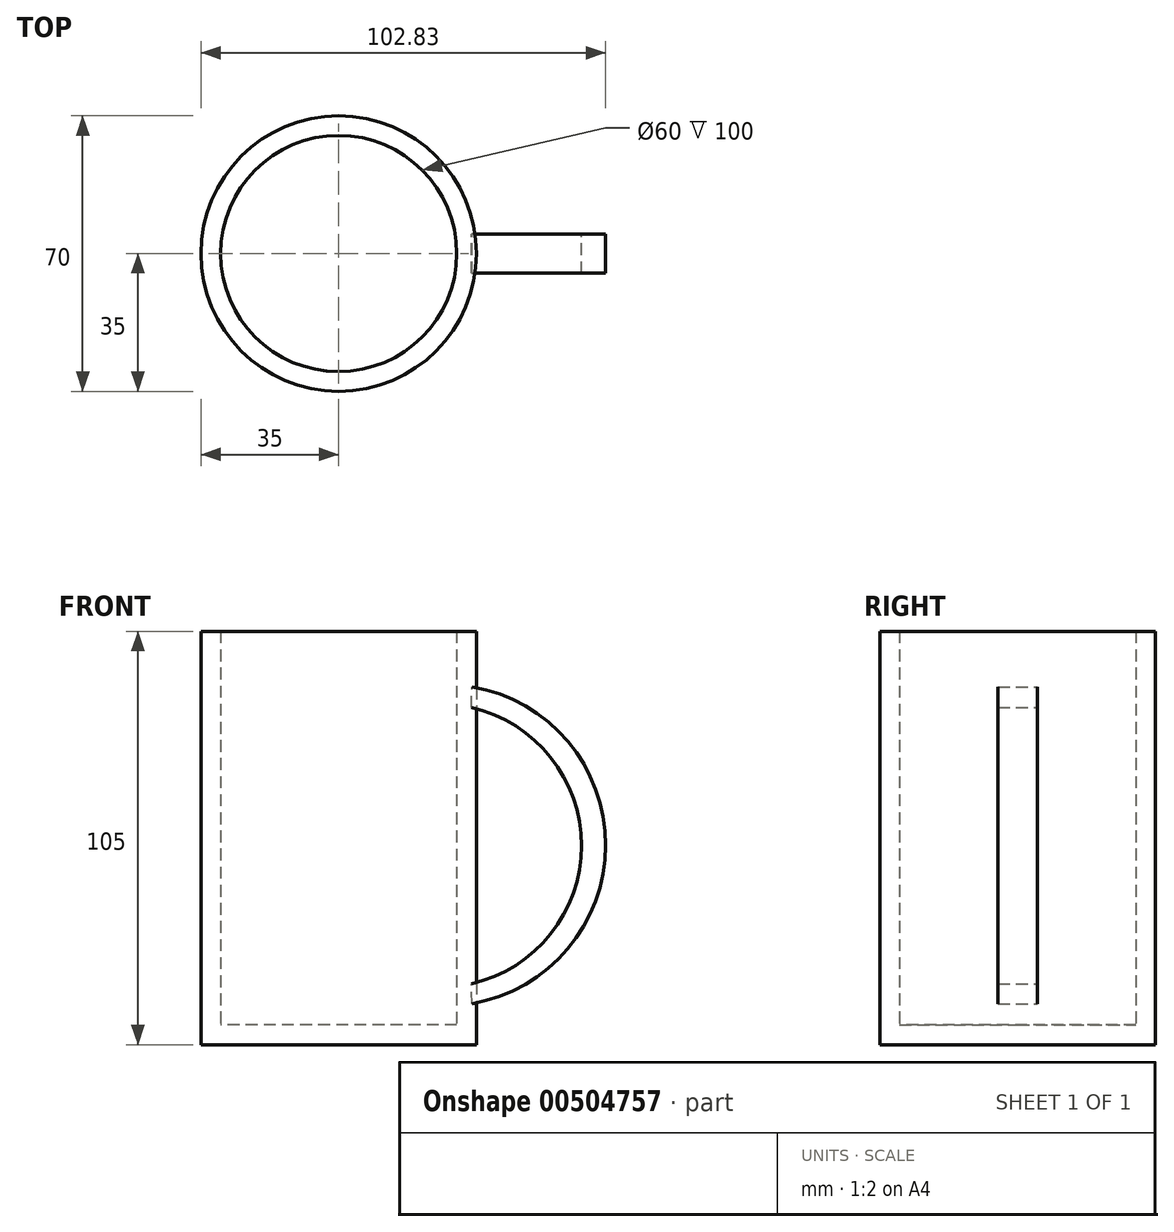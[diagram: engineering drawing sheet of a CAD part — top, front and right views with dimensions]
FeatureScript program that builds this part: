
annotation { "Feature Type Name" : "Feature", "Feature Type Description" : "" }
export const myFeature = defineFeature(function(context is Context, id is Id, definition is map)
    precondition{}
    {
        {
            var Q0;
            Q0=qCreatedBy(makeId("Top.planeOp"),FACE);
            var sketch = newSketch(context, id + "F0", { "sketchPlane" : qUnion([Q0])});
            skCircle(sketch, "E0", {"center": v(0, 0) * mm, "radius": 35 * mm});
            skSolve(sketch);
        }
        {
            var Q0;
            Q0 = qSketchRegion(id + "F0", true);
            extrude(context, id + "F1", {"entities" : qUnion([Q0]), "depth" : 5 * mm});
        }
        {
            var Q0;
            Q0=makeQuery(id+"F1.opExtrude","CAP_FACE",FACE,{"disambiguationData":[OSD([sQuery(id+"F0.wireOp",EDGE,"E0")])],"isStart":false});
            var sketch = newSketch(context, id + "F2", { "sketchPlane" : qUnion([Q0])});
            skCircle(sketch, "E1", {"center": v(0, 0) * mm, "radius": 35 * mm});
            skCircle(sketch, "E2", {"center": v(0, 0) * mm, "radius": 30 * mm});
            skSolve(sketch);
        }
        {
            var Q0;
            Q0 = qSketchRegion(id + "F2", true);
            extrude(context, id + "F3", {"entities" : qUnion([Q0]), "operationType" : NewBodyOperationType.ADD, "depth" : 100 * mm});
        }
        {
            var Q0;
            Q0=qCreatedBy(makeId("Front.planeOp"),FACE);
            var sketch = newSketch(context, id + "F4", { "sketchPlane" : qUnion([Q0])});
            skArc(sketch, "E3", {"start": v(33.72, 15.46) * mm, "mid": v(61.72, 50.56) * mm, "end": v(33.73, 85.66) * mm});
            skArc(sketch, "E4", {"start": v(33.82, 10.41) * mm, "mid": v(67.83, 50.65) * mm, "end": v(33.88, 90.94) * mm});
            skLineSegment(sketch, "E5", {"start": v(33.73, 85.66) * mm, "end": v(33.88, 90.94) * mm});
            skLineSegment(sketch, "E6", {"start": v(33.82, 10.41) * mm, "end": v(33.72, 15.46) * mm});
            skSolve(sketch);
        }
        {
            var Q0;
            Q0 = qSketchRegion(id + "F4", true);
            extrude(context, id + "F5", {"entities" : qUnion([Q0]), "endBound" : BoundingType.SYMMETRIC, "depth" : 10 * mm});
        }
    });
